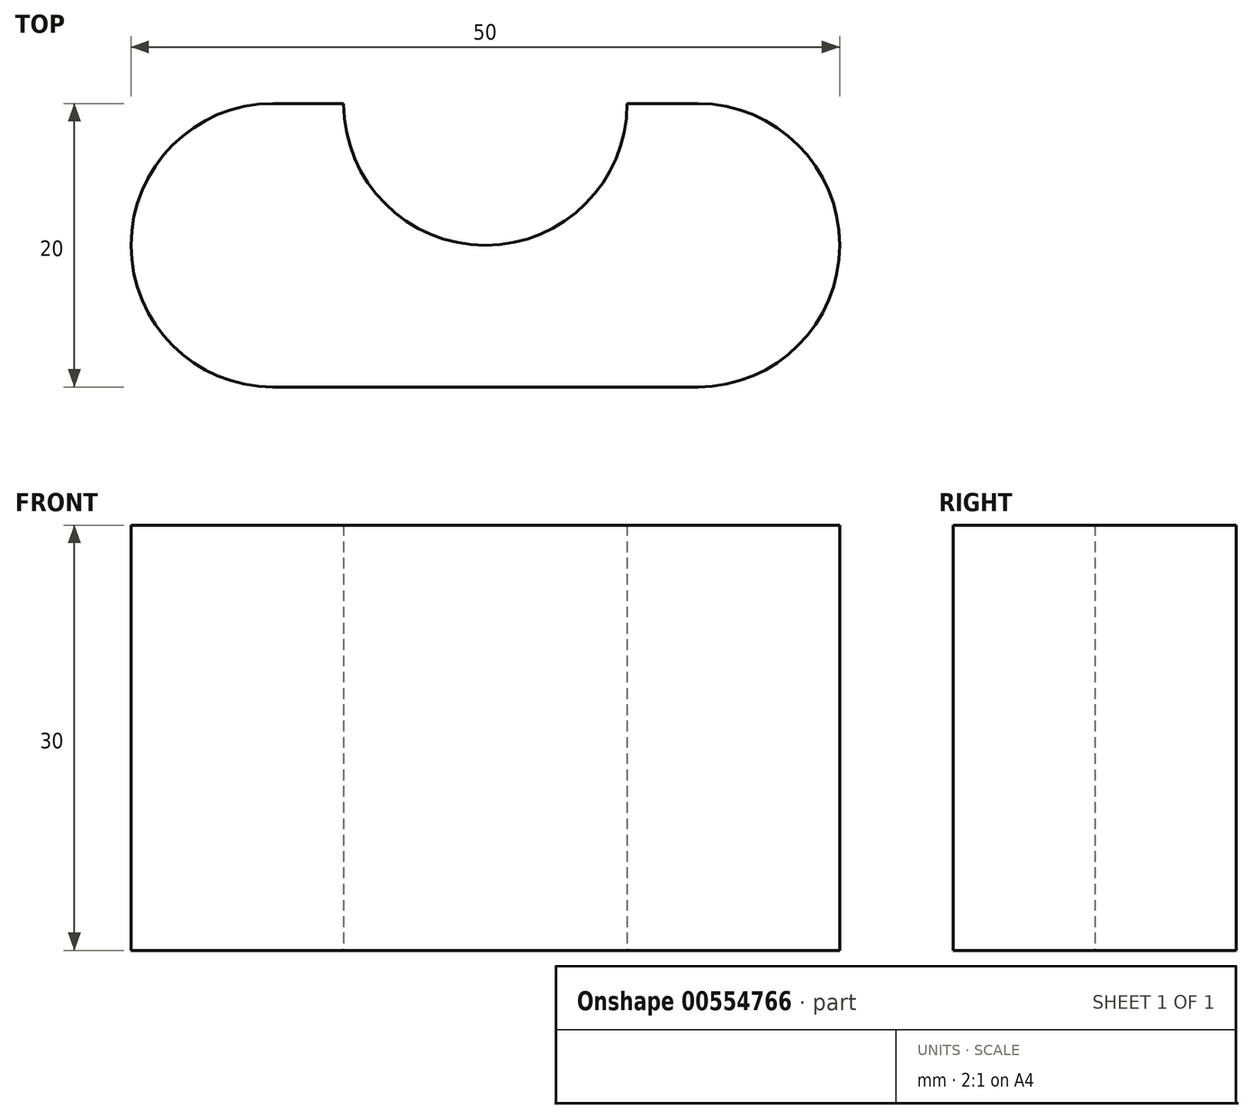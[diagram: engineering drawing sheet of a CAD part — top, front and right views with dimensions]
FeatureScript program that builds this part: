
annotation { "Feature Type Name" : "Feature", "Feature Type Description" : "" }
export const myFeature = defineFeature(function(context is Context, id is Id, definition is map)
    precondition{}
    {
        {
            var Q0;
            Q0=qCreatedBy(makeId("Top.planeOp"),FACE);
            var sketch = newSketch(context, id + "F0", { "sketchPlane" : qUnion([Q0])});
            skArc(sketch, "E0", {"start": v(-9.37, 10) * mm, "mid": v(0.63, 0) * mm, "end": v(10.63, 10) * mm});
            skArc(sketch, "E1", {"start": v(15.63, -10) * mm, "mid": v(25.63, 0) * mm, "end": v(15.63, 10) * mm});
            skArc(sketch, "E2", {"start": v(-14.37, 10) * mm, "mid": v(-24.37, 0) * mm, "end": v(-14.37, -10) * mm});
            skLineSegment(sketch, "E3", {"start": v(-14.37, -10) * mm, "end": v(15.63, -10) * mm});
            skLineSegment(sketch, "E4", {"start": v(-14.37, 10) * mm, "end": v(-9.37, 10) * mm});
            skLineSegment(sketch, "E5.trimOffspring", {"start": v(10.63, 10) * mm, "end": v(15.63, 10) * mm});
            skSolve(sketch);
        }
        {
            var Q0;
            Q0 = qSketchRegion(id + "F0", true);
            extrude(context, id + "F1", {"entities" : qUnion([Q0]), "depth" : 30 * mm, "offsetDistance" : 25 * mm});
        }
    });
